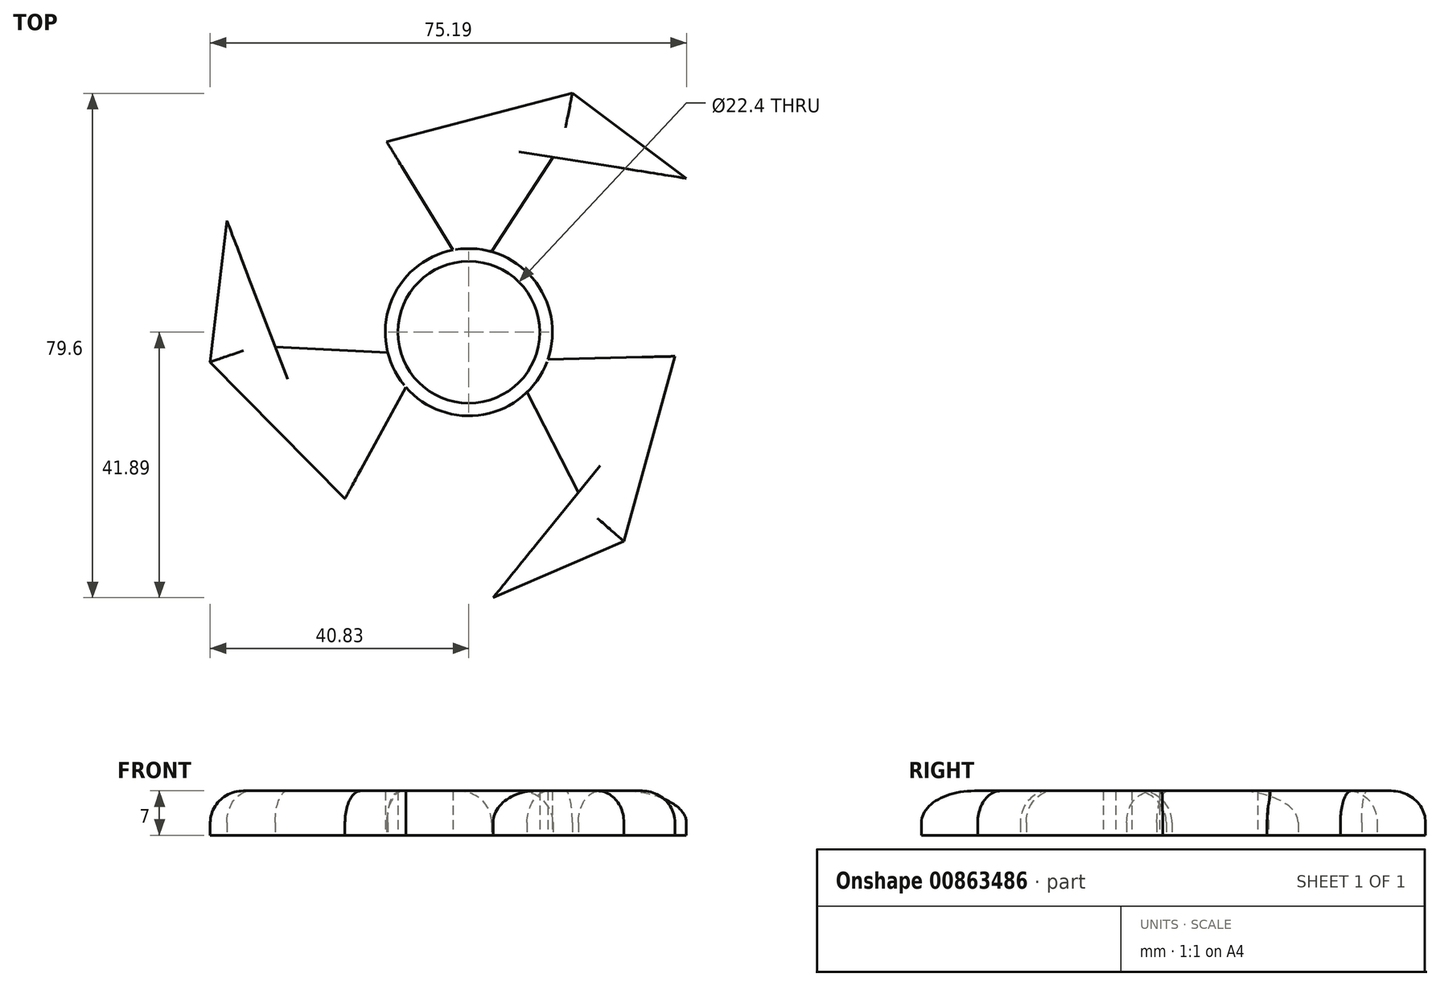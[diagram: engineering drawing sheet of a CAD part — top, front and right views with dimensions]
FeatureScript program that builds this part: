
annotation { "Feature Type Name" : "Feature", "Feature Type Description" : "" }
export const myFeature = defineFeature(function(context is Context, id is Id, definition is map)
    precondition{}
    {
        {
            var Q0;
            Q0=qCreatedBy(makeId("Top.planeOp"),FACE);
            var sketch = newSketch(context, id + "F0", { "sketchPlane" : qUnion([Q0])});
            skCircle(sketch, "E0", {"center": v(0, 0) * mm, "radius": 11.2 * mm});
            skCircle(sketch, "E1", {"center": v(0, 0) * mm, "radius": 13.2 * mm});
            skLineSegment(sketch, "E2", {"start": v(-2.52, 12.96) * mm, "end": v(-12.98, 30.08) * mm});
            skLineSegment(sketch, "E3", {"start": v(-12.98, 30.08) * mm, "end": v(16.34, 37.71) * mm});
            skLineSegment(sketch, "E4", {"start": v(16.34, 37.71) * mm, "end": v(34.36, 24.28) * mm});
            skLineSegment(sketch, "E5", {"start": v(34.36, 24.28) * mm, "end": v(13.28, 27.64) * mm});
            skLineSegment(sketch, "E6", {"start": v(13.28, 27.64) * mm, "end": v(3.6, 12.7) * mm});
            skLineSegment(sketch, "E7.1.0", {"start": v(-19.56, -26.28) * mm, "end": v(-40.83, -4.7) * mm});
            skLineSegment(sketch, "E7.1.1", {"start": v(-9.96, -8.66) * mm, "end": v(-19.56, -26.28) * mm});
            skLineSegment(sketch, "E7.1.2", {"start": v(-30.58, -2.31) * mm, "end": v(-12.8, -3.23) * mm});
            skLineSegment(sketch, "E7.1.3", {"start": v(-38.2, 17.61) * mm, "end": v(-30.58, -2.31) * mm});
            skLineSegment(sketch, "E7.1.4", {"start": v(-40.83, -4.7) * mm, "end": v(-38.2, 17.61) * mm});
            skLineSegment(sketch, "E7.2.0", {"start": v(32.54, -3.8) * mm, "end": v(24.5, -33) * mm});
            skLineSegment(sketch, "E7.2.1", {"start": v(12.48, -4.3) * mm, "end": v(32.54, -3.8) * mm});
            skLineSegment(sketch, "E7.2.2", {"start": v(17.3, -25.32) * mm, "end": v(9.2, -9.47) * mm});
            skLineSegment(sketch, "E7.2.3", {"start": v(3.85, -41.9) * mm, "end": v(17.3, -25.32) * mm});
            skLineSegment(sketch, "E7.2.4", {"start": v(24.5, -33) * mm, "end": v(3.85, -41.9) * mm});
            skSolve(sketch);
        }
        {
            var Q0;
            Q0 = qSketchRegion(id + "F0", true);
            extrude(context, id + "F1", {"entities" : qUnion([Q0]), "depth" : 7 * mm, "offsetDistance" : 25 * mm});
        }
        {
            var Q0;
            Q0=makeQuery(id+"F1.opExtrude","CAP_EDGE",EDGE,{"disambiguationData":[OSD([sQuery(id+"F0.wireOp",EDGE,"E7.1.4")])],"isStart":false});
            var Q1;
            Q1=makeQuery(id+"F1.opExtrude","CAP_EDGE",EDGE,{"disambiguationData":[OSD([sQuery(id+"F0.wireOp",EDGE,"E7.2.4")])],"isStart":false});
            var Q2;
            Q2=makeQuery(id+"F1.opExtrude","CAP_EDGE",EDGE,{"disambiguationData":[OSD([sQuery(id+"F0.wireOp",EDGE,"E4")])],"isStart":false});
            var Q3;
            Q3=makeQuery(id+"F1.opExtrude","CAP_EDGE",EDGE,{"disambiguationData":[OSD([sQuery(id+"F0.wireOp",EDGE,"E7.1.2")])],"isStart":false});
            var Q4;
            Q4=makeQuery(id+"F1.opExtrude","CAP_EDGE",EDGE,{"disambiguationData":[OSD([sQuery(id+"F0.wireOp",EDGE,"E6")])],"isStart":false});
            var Q5;
            Q5=makeQuery(id+"F1.opExtrude","CAP_EDGE",EDGE,{"disambiguationData":[OSD([sQuery(id+"F0.wireOp",EDGE,"E3")])],"isStart":false});
            var Q6;
            Q6=makeQuery(id+"F1.opExtrude","CAP_EDGE",EDGE,{"disambiguationData":[OSD([sQuery(id+"F0.wireOp",EDGE,"E7.1.0")])],"isStart":false});
            var Q7;
            Q7=makeQuery(id+"F1.opExtrude","CAP_EDGE",EDGE,{"disambiguationData":[OSD([sQuery(id+"F0.wireOp",EDGE,"E7.2.0")])],"isStart":false});
            var Q8;
            Q8=makeQuery(id+"F1.opExtrude","CAP_EDGE",EDGE,{"disambiguationData":[OSD([sQuery(id+"F0.wireOp",EDGE,"E7.2.2")])],"isStart":false});
            fillet(context, id + "F2", {"entities" : qUnion([Q0, Q1, Q2, Q3, Q4, Q5, Q6, Q7, Q8]), "radius" : 5 * mm, "tangentPropagation" : true, "allowEdgeOverflow" : false});
        }
    });
